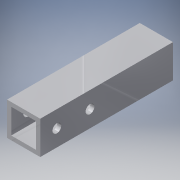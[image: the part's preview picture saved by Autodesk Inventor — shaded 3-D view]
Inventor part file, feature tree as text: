
AUTODESK INVENTOR PART (.ipt)
format: ipt  version: 2016 (Build 200138000, 138)  size: 123,904 bytes
history: native  units: in
note: dims shown in document units (in); Inventor stores cm internally (conversion verified against a paired STEP export)
features: extrude x2, sketch x2
ambient origin geometry x8: Origin, YZ Plane, XZ Plane, XY Plane, X Axis, Y Axis, Z Axis, Center Point
bodies: Solid1 (feature_tree)
feature tree (4):
  extrude  "Extrusion1"  Depth=2.0in
  extrude  "Extrusion3"  Depth=0.125in
  sketch  "Sketch1"  dims[d0=1.0in d1=2.0in]
  sketch  "Sketch2"  dims[d2=0.125in d3=0.125in d4=0.125in d5=0.125in d6=4.0in d7=0.0in d8=0.2656in d12=2.5in d13=3.5in d14=0.5in d17=1.5in d18=1.0in d19=0.0in d27=0.6in d28=0.5in d29=1.5in d30=0.5in]
